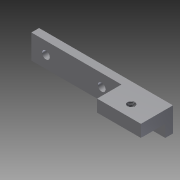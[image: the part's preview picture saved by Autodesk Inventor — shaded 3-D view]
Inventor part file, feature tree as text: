
AUTODESK INVENTOR PART (.ipt)
format: ipt  version: 2011 (Build 150239000, 239)  size: 111,616 bytes
history: native  units: in
note: dims shown in document units (in); Inventor stores cm internally (conversion verified against a paired STEP export)
features: sketch x5, extrude x3, hole x2, thread x1
ambient origin geometry x8: Origin, YZ Plane, XZ Plane, XY Plane, X Axis, Y Axis, Z Axis, Center Point
bodies: Solid1 (feature_tree)
feature tree (11):
  extrude  "Extrusion1"  Depth=0.3937in
  hole  "Hole1"  [1 undecoded]
  extrude  "Extrusion4"  Depth=0.7087in
  hole  "Hole3"  [1 undecoded]
  thread  "Thread2"  [1 undecoded]
  extrude  "Extrusion5"  Depth=0.0157in
  sketch  "Sketch1"  dims[d0=2.1654in d1=0.3937in]
  sketch  "Sketch3"  dims[d2=0.125in d3=0.0in d8=0.2362in]
  sketch  "Sketch6"  dims[d9=0.9016in]
  sketch  "Sketch7"  dims[d10=0.126in d11=0.75in d12=0.375in d13=0.25in d14=0.5635in d15=1.0in d16=0.8108in d32=0.7087in]
  sketch  "Sketch8"  dims[d33=0.1969in d34=0.3937in d35=0.0in d36=0.1181in d37=0.75in d38=0.375in d39=0.25in d40=0.5635in d41=1.0in d42=0.8108in d43=1.0in d44=0.0in d45=0.0157in d46=0.0079in d47=45.0deg d48=135.0deg d49=0.3937in d50=0.0in]
note: 3 required parameter values undecoded (feature->parameter linkage not recoverable at this tier; creation-order binding heuristic only, values carry confidence <= 0.55)
